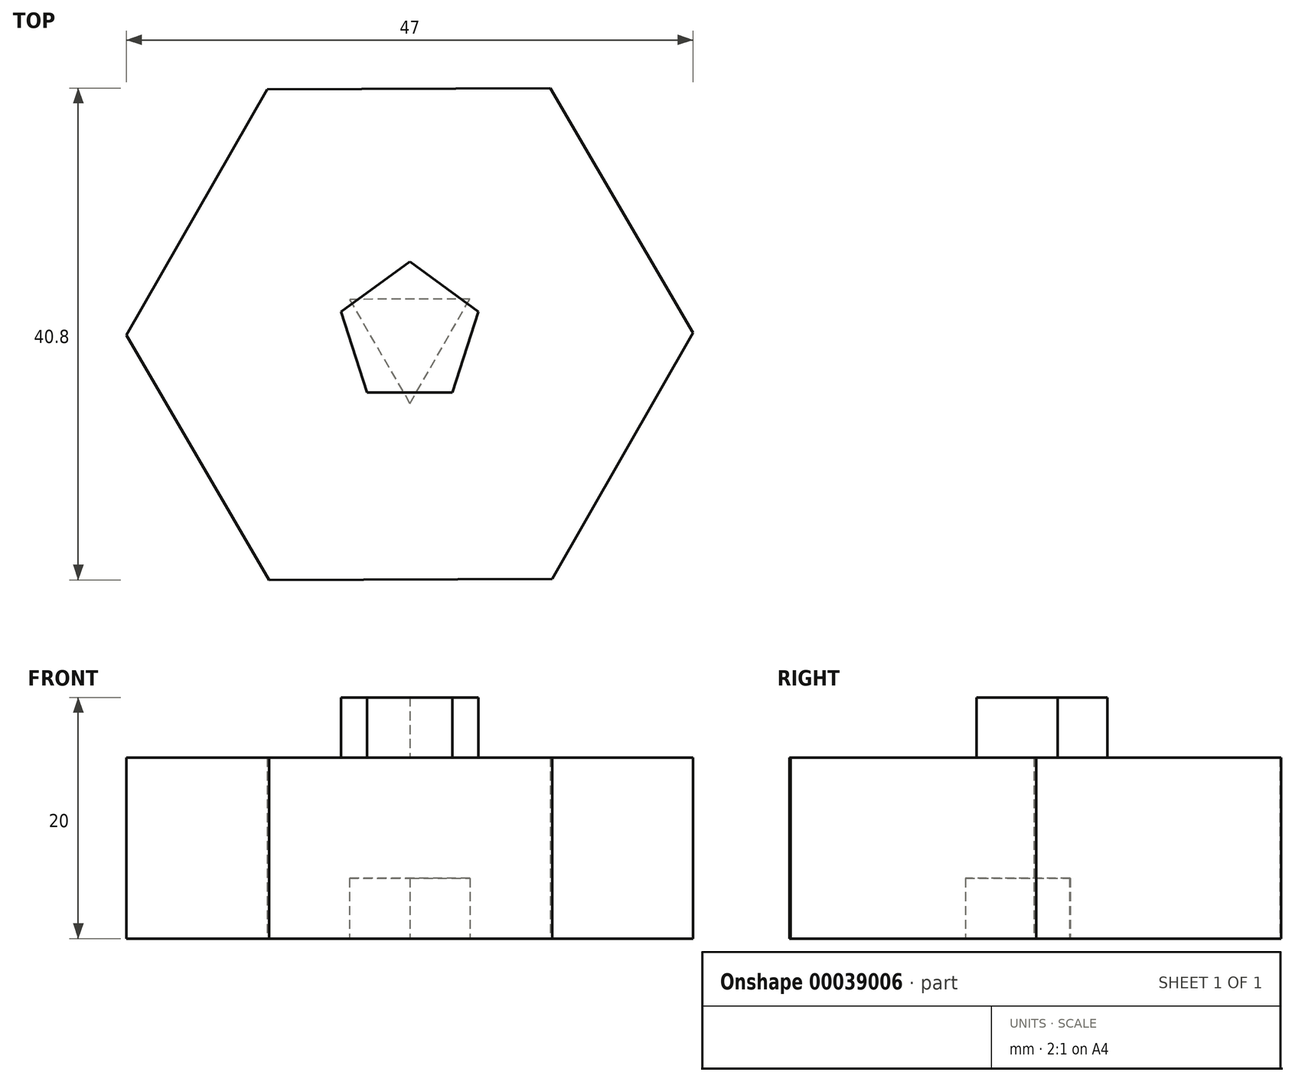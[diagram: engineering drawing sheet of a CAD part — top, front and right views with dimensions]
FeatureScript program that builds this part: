
annotation { "Feature Type Name" : "Feature", "Feature Type Description" : "" }
export const myFeature = defineFeature(function(context is Context, id is Id, definition is map)
    precondition{}
    {
        {
            var Q0;
            Q0=qCreatedBy(makeId("Top.planeOp"),FACE);
            var sketch = newSketch(context, id + "F0", { "sketchPlane" : qUnion([Q0])});
            skCircle(sketch, "E0.cCircle", {"center": v(0, 0) * mm, "radius": 20.35 * mm, "construction": true});
            skLineSegment(sketch, "E0.0", {"start": v(-23.5, -0.1) * mm, "end": v(-11.83, 20.3) * mm});
            skLineSegment(sketch, "E0.1", {"start": v(-11.83, 20.3) * mm, "end": v(11.67, 20.4) * mm});
            skLineSegment(sketch, "E0.2", {"start": v(11.67, 20.4) * mm, "end": v(23.5, 0.1) * mm});
            skLineSegment(sketch, "E0.3", {"start": v(23.5, 0.1) * mm, "end": v(11.83, -20.3) * mm});
            skLineSegment(sketch, "E0.4", {"start": v(11.83, -20.3) * mm, "end": v(-11.67, -20.4) * mm});
            skLineSegment(sketch, "E0.5", {"start": v(-11.67, -20.4) * mm, "end": v(-23.5, -0.1) * mm});
            skPoint(sketch, "E0.0.midPoint", {"position": v(-17.66, 10.1) * mm});
            skLineSegment(sketch, "E1", {"start": v(0, -7.16) * mm, "end": v(1.77, -7.16) * mm});
            skLineSegment(sketch, "E2", {"start": v(1.77, -7.16) * mm, "end": v(3.53, -13.44) * mm});
            skLineSegment(sketch, "E3", {"start": v(3.53, -13.44) * mm, "end": v(-1.77, -13.44) * mm});
            skLineSegment(sketch, "E4", {"start": v(-8.15, 2.36) * mm, "end": v(-8.15, -1.57) * mm});
            skLineSegment(sketch, "E5", {"start": v(-8.15, -1.57) * mm, "end": v(-15.21, -3.73) * mm});
            skLineSegment(sketch, "E6", {"start": v(-15.21, -3.73) * mm, "end": v(-11.68, -2.65) * mm});
            skLineSegment(sketch, "E7", {"start": v(-11.68, -2.65) * mm, "end": v(-11.68, 0) * mm});
            skLineSegment(sketch, "E8", {"start": v(-11.68, 0) * mm, "end": v(-15.21, 2.36) * mm});
            skLineSegment(sketch, "E9", {"start": v(4.12, 8.93) * mm, "end": v(-4.12, 8.93) * mm});
            skLineSegment(sketch, "E10", {"start": v(-4.12, 8.93) * mm, "end": v(-4.12, 15.8) * mm});
            skLineSegment(sketch, "E11", {"start": v(1.77, 12.86) * mm, "end": v(1.77, 15.8) * mm});
            skLineSegment(sketch, "E12", {"start": v(8.34, -6.48) * mm, "end": v(8.34, -1.77) * mm});
            skLineSegment(sketch, "E13", {"start": v(8.34, -1.77) * mm, "end": v(11.09, 2.75) * mm});
            skLineSegment(sketch, "E14", {"start": v(11.09, 2.75) * mm, "end": v(17.17, 2.75) * mm});
            skLineSegment(sketch, "E15", {"start": v(17.17, 2.75) * mm, "end": v(20.24, -2.16) * mm});
            skLineSegment(sketch, "E16", {"start": v(20.24, -2.16) * mm, "end": v(16.39, -6.28) * mm});
            skLineSegment(sketch, "E17", {"start": v(16.39, -6.28) * mm, "end": v(14.62, -2.75) * mm});
            skLineSegment(sketch, "E18", {"start": v(14.62, -2.75) * mm, "end": v(16.66, -1.73) * mm});
            skSolve(sketch);
        }
        {
            var Q0;
            Q0=makeQuery(id+"F0.imprint","IMPRINT",FACE,{"disambiguationData":[TD([[makeQuery(id+"F0.imprint","IMPRINT",EDGE,{"derivedFrom":sQuery(id+"F0.wireOp",EDGE,"E0.0")}),-1.0]])]});
            extrude(context, id + "F1", {"entities" : qUnion([Q0]), "depth" : 15 * mm});
        }
        {
            var Q0;
            Q0=makeQuery(id+"F1.opExtrude","CAP_FACE",FACE,{"disambiguationData":[OSD([sQuery(id+"F0.wireOp",EDGE,"E0.0"),sQuery(id+"F0.wireOp",EDGE,"E0.1"),sQuery(id+"F0.wireOp",EDGE,"E0.2"),sQuery(id+"F0.wireOp",EDGE,"E0.3"),sQuery(id+"F0.wireOp",EDGE,"E0.4"),sQuery(id+"F0.wireOp",EDGE,"E0.5")])],"isStart":false});
            var sketch = newSketch(context, id + "F2", { "sketchPlane" : qUnion([Q0])});
            skCircle(sketch, "E19.cCircle", {"center": v(0, 0) * mm, "radius": 4.85 * mm, "construction": true});
            skLineSegment(sketch, "E19.0", {"start": v(3.53, -4.85) * mm, "end": v(-3.53, -4.85) * mm});
            skLineSegment(sketch, "E19.1", {"start": v(-3.53, -4.85) * mm, "end": v(-5.7, 1.85) * mm});
            skLineSegment(sketch, "E19.2", {"start": v(-5.7, 1.85) * mm, "end": v(0, 6) * mm});
            skLineSegment(sketch, "E19.3", {"start": v(0, 6) * mm, "end": v(5.7, 1.85) * mm});
            skLineSegment(sketch, "E19.4", {"start": v(5.7, 1.85) * mm, "end": v(3.53, -4.85) * mm});
            skPoint(sketch, "E19.0.midPoint", {"position": v(0, -4.85) * mm});
            skSolve(sketch);
        }
        {
            var Q0;
            Q0=makeQuery(id+"F2.imprint","IMPRINT",FACE,{"disambiguationData":[TD([[makeQuery(id+"F2.imprint","IMPRINT",EDGE,{"derivedFrom":sQuery(id+"F2.wireOp",EDGE,"E19.0")}),-1.0]])]});
            extrude(context, id + "F3", {"entities" : qUnion([Q0]), "operationType" : NewBodyOperationType.ADD, "endBound" : BoundingType.SYMMETRIC, "depth" : 10 * mm});
        }
        {
            var Q0;
            Q0=makeQuery(id+"F1.opExtrude","CAP_FACE",FACE,{"disambiguationData":[OSD([sQuery(id+"F0.wireOp",EDGE,"E0.0"),sQuery(id+"F0.wireOp",EDGE,"E0.1"),sQuery(id+"F0.wireOp",EDGE,"E0.2"),sQuery(id+"F0.wireOp",EDGE,"E0.3"),sQuery(id+"F0.wireOp",EDGE,"E0.4"),sQuery(id+"F0.wireOp",EDGE,"E0.5")])],"isStart":true});
            var sketch = newSketch(context, id + "F4", { "sketchPlane" : qUnion([Q0])});
            skCircle(sketch, "E20.cCircle", {"center": v(0, 0) * mm, "radius": 2.89 * mm, "construction": true});
            skLineSegment(sketch, "E20.0", {"start": v(4.99, -2.9) * mm, "end": v(-5.01, -2.87) * mm});
            skLineSegment(sketch, "E20.1", {"start": v(-5.01, -2.87) * mm, "end": v(0.02, 5.77) * mm});
            skLineSegment(sketch, "E20.2", {"start": v(0.02, 5.77) * mm, "end": v(4.99, -2.9) * mm});
            skPoint(sketch, "E20.0.midPoint", {"position": v(-0.01, -2.89) * mm});
            skSolve(sketch);
        }
        {
            var Q0;
            Q0 = qSketchRegion(id + "F4", true);
            extrude(context, id + "F5", {"entities" : qUnion([Q0]), "operationType" : NewBodyOperationType.REMOVE, "oppositeDirection" : true, "depth" : 5 * mm});
        }
    });
